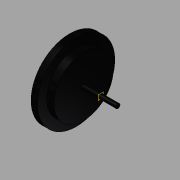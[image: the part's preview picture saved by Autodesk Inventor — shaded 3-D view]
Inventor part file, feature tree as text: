
AUTODESK INVENTOR PART (.ipt)
format: ipt  version: 2015 (Build 190159000, 159)  size: 142,336 bytes
history: native  units: in
note: dims shown in document units (in); Inventor stores cm internally (conversion verified against a paired STEP export)
features: sketch x5, other x3, plane x1
ambient origin geometry x8: Origin, YZ Plane, XZ Plane, XY Plane, X Axis, Y Axis, Z Axis, Center Point
bodies: Solid1 (feature_tree)
feature tree (9):
  other  "rueda_MIR1.ipt"
  other  "Solid1::rueda_MIR1.ipt"
  other  "TaggingFeature1"
  sketch  "Sketch2"  dims[d0=0.3937in]
  sketch  "Sketch3"
  sketch  "Sketch7"
  sketch  "Sketch12"
  sketch  "Sketch13"
  plane  "Work Plane1"
